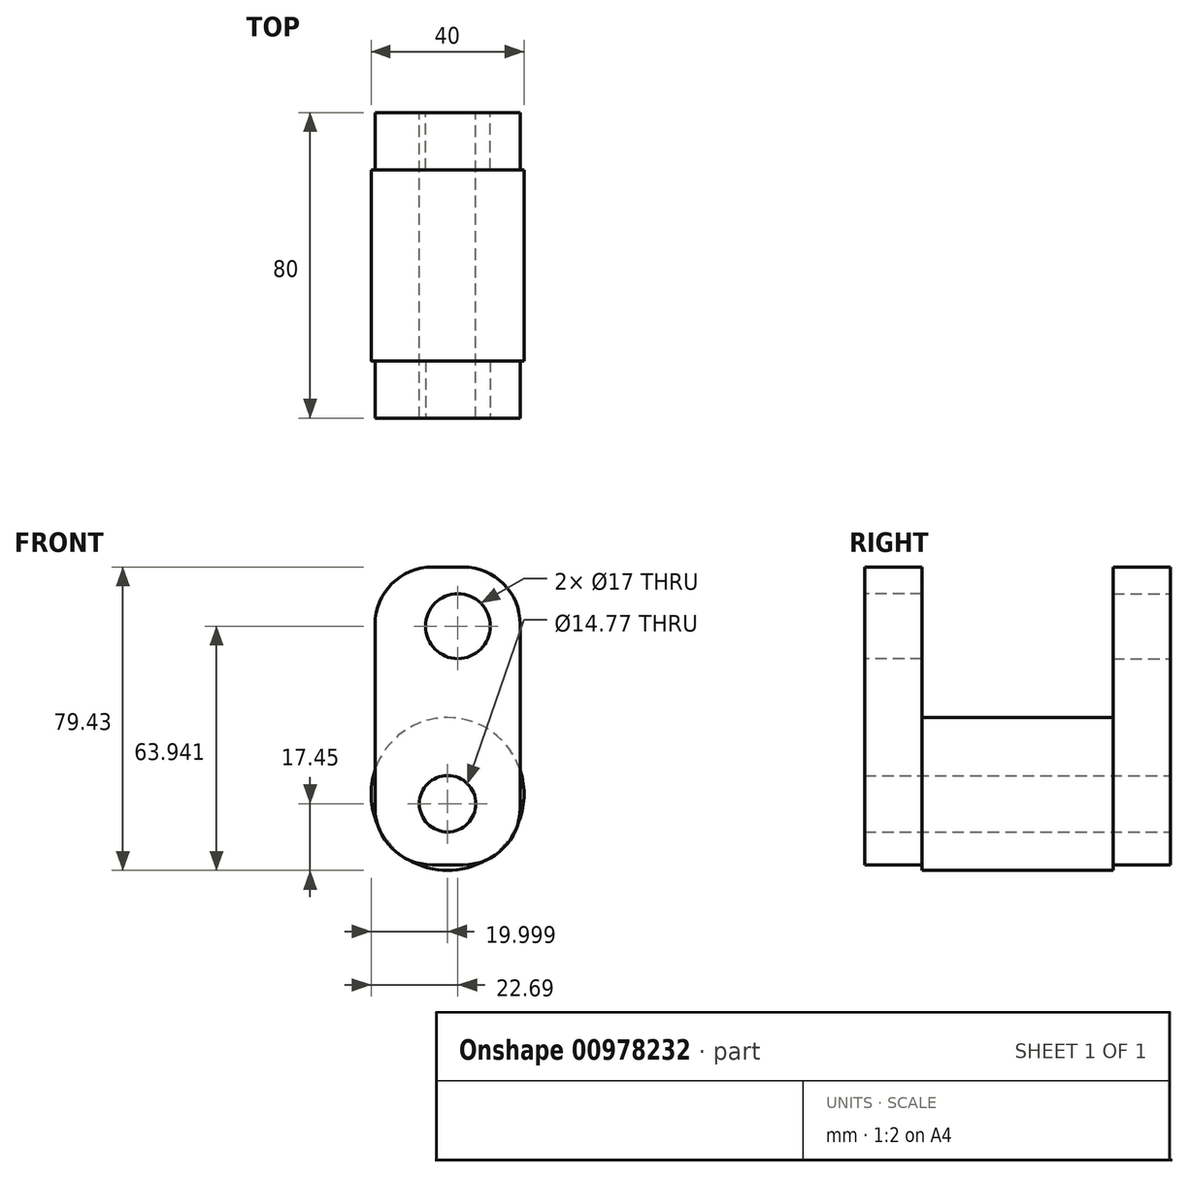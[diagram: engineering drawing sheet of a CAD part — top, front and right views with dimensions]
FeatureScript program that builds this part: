
annotation { "Feature Type Name" : "Feature", "Feature Type Description" : "" }
export const myFeature = defineFeature(function(context is Context, id is Id, definition is map)
    precondition{}
    {
        {
            var Q0;
            Q0=qCreatedBy(makeId("Front.planeOp"),FACE);
            var sketch = newSketch(context, id + "F0", { "sketchPlane" : qUnion([Q0])});
            skCircle(sketch, "E0", {"center": v(-2.7, 9.49) * mm, "radius": 20 * mm});
            skSolve(sketch);
        }
        {
            var Q0;
            Q0=makeQuery(id+"F0.imprint","IMPRINT",FACE,{"disambiguationData":[TD([[makeQuery(id+"F0.imprint","IMPRINT",EDGE,{"derivedFrom":sQuery(id+"F0.wireOp",EDGE,"E0")}),1.0]])]});
            extrude(context, id + "F1", {"entities" : qUnion([Q0]), "depth" : 25 * mm, "offsetDistance" : 25 * mm});
        }
        {
            var Q0;
            Q0=makeQuery(id+"F1.opExtrude","CAP_FACE",FACE,{"disambiguationData":[OSD([sQuery(id+"F0.wireOp",EDGE,"E0")])],"isStart":true});
            var sketch = newSketch(context, id + "F2", { "sketchPlane" : qUnion([Q0])});
            skLineSegment(sketch, "E1.bottom", {"start": v(-1.32, -9.08) * mm, "end": v(6.68, -9.08) * mm});
            skLineSegment(sketch, "E1.top", {"start": v(-1.32, 68.92) * mm, "end": v(6.68, 68.92) * mm});
            skLineSegment(sketch, "E1.left", {"start": v(-16.32, 5.92) * mm, "end": v(-16.32, 53.92) * mm});
            skLineSegment(sketch, "E1.right", {"start": v(21.68, 5.92) * mm, "end": v(21.68, 53.92) * mm});
            skPoint(sketch, "E2.visualSharp", {"position": v(-16.32, -9.08) * mm});
            skArc(sketch, "E2.filletArc", {"start": v(-16.32, 5.92) * mm, "mid": v(-11.92, -4.69) * mm, "end": v(-1.32, -9.08) * mm});
            skPoint(sketch, "E3.visualSharp", {"position": v(21.68, -9.08) * mm});
            skArc(sketch, "E3.filletArc", {"start": v(6.68, -9.08) * mm, "mid": v(17.3, -4.69) * mm, "end": v(21.68, 5.92) * mm});
            skPoint(sketch, "E4.visualSharp", {"position": v(21.68, 68.92) * mm});
            skArc(sketch, "E4.filletArc", {"start": v(21.68, 53.92) * mm, "mid": v(17.3, 64.53) * mm, "end": v(6.68, 68.92) * mm});
            skPoint(sketch, "E5.visualSharp", {"position": v(-16.32, 68.92) * mm});
            skArc(sketch, "E5.filletArc", {"start": v(-1.32, 68.92) * mm, "mid": v(-11.92, 64.53) * mm, "end": v(-16.32, 53.92) * mm});
            skSolve(sketch);
        }
        {
            var Q0;
            Q0 = qSketchRegion(id + "F2", true);
            extrude(context, id + "F3", {"entities" : qUnion([Q0]), "operationType" : NewBodyOperationType.ADD, "depth" : 15 * mm, "offsetDistance" : 25 * mm});
        }
        {
            var Q0;
            Q0=makeQuery(id+"F3.opExtrude","CAP_FACE",FACE,{"disambiguationData":[OSD([sQuery(id+"F2.wireOp",EDGE,"E1.bottom"),sQuery(id+"F2.wireOp",EDGE,"E1.top"),sQuery(id+"F2.wireOp",EDGE,"E1.left"),sQuery(id+"F2.wireOp",EDGE,"E1.right"),sQuery(id+"F2.wireOp",EDGE,"E2.filletArc"),sQuery(id+"F2.wireOp",EDGE,"E3.filletArc"),sQuery(id+"F2.wireOp",EDGE,"E4.filletArc"),sQuery(id+"F2.wireOp",EDGE,"E5.filletArc")])],"isStart":false});
            var sketch = newSketch(context, id + "F4", { "sketchPlane" : qUnion([Q0])});
            skCircle(sketch, "E6", {"center": v(2.7, 6.94) * mm, "radius": 7.39 * mm});
            skSolve(sketch);
        }
        {
            var Q0;
            Q0=makeQuery(id+"F4.imprint","IMPRINT",FACE,{"disambiguationData":[TD([[makeQuery(id+"F4.imprint","IMPRINT",EDGE,{"derivedFrom":sQuery(id+"F4.wireOp",EDGE,"E6")}),1.0]])]});
            extrude(context, id + "F5", {"entities" : qUnion([Q0]), "operationType" : NewBodyOperationType.REMOVE, "oppositeDirection" : true, "depth" : 125 * mm, "offsetDistance" : 25 * mm});
        }
        {
            var Q0;
            Q0=makeQuery(id+"F3.opExtrude","CAP_FACE",FACE,{"disambiguationData":[OSD([sQuery(id+"F2.wireOp",EDGE,"E1.bottom"),sQuery(id+"F2.wireOp",EDGE,"E1.top"),sQuery(id+"F2.wireOp",EDGE,"E1.left"),sQuery(id+"F2.wireOp",EDGE,"E1.right"),sQuery(id+"F2.wireOp",EDGE,"E2.filletArc"),sQuery(id+"F2.wireOp",EDGE,"E3.filletArc"),sQuery(id+"F2.wireOp",EDGE,"E4.filletArc"),sQuery(id+"F2.wireOp",EDGE,"E5.filletArc")])],"isStart":false});
            var sketch = newSketch(context, id + "F6", { "sketchPlane" : qUnion([Q0])});
            skCircle(sketch, "E7", {"center": v(0, 53.43) * mm, "radius": 8.5 * mm});
            skSolve(sketch);
        }
        {
            var Q0;
            Q0=makeQuery(id+"F6.imprint","IMPRINT",FACE,{"disambiguationData":[TD([[makeQuery(id+"F6.imprint","IMPRINT",EDGE,{"derivedFrom":sQuery(id+"F6.wireOp",EDGE,"E7")}),1.0]])]});
            extrude(context, id + "F7", {"entities" : qUnion([Q0]), "operationType" : NewBodyOperationType.REMOVE, "oppositeDirection" : true, "depth" : 25 * mm, "offsetDistance" : 25 * mm});
        }
        {
            var Q0;
            Q0=makeQuery(id+"F1.opExtrude","SWEPT_BODY",BODY,{"disambiguationData":[OSD([sQuery(id+"F0.wireOp",EDGE,"E0")])]});
            var Q1;
            Q1=makeQuery(id+"F1.opExtrude","CAP_FACE",FACE,{"disambiguationData":[OSD([sQuery(id+"F0.wireOp",EDGE,"E0")])],"isStart":false});
            mirror(context, id + "F8", {"operationType" : NewBodyOperationType.ADD, "entities" : qUnion([Q0]), "mirrorPlane" : qUnion([Q1])});
        }
    });
